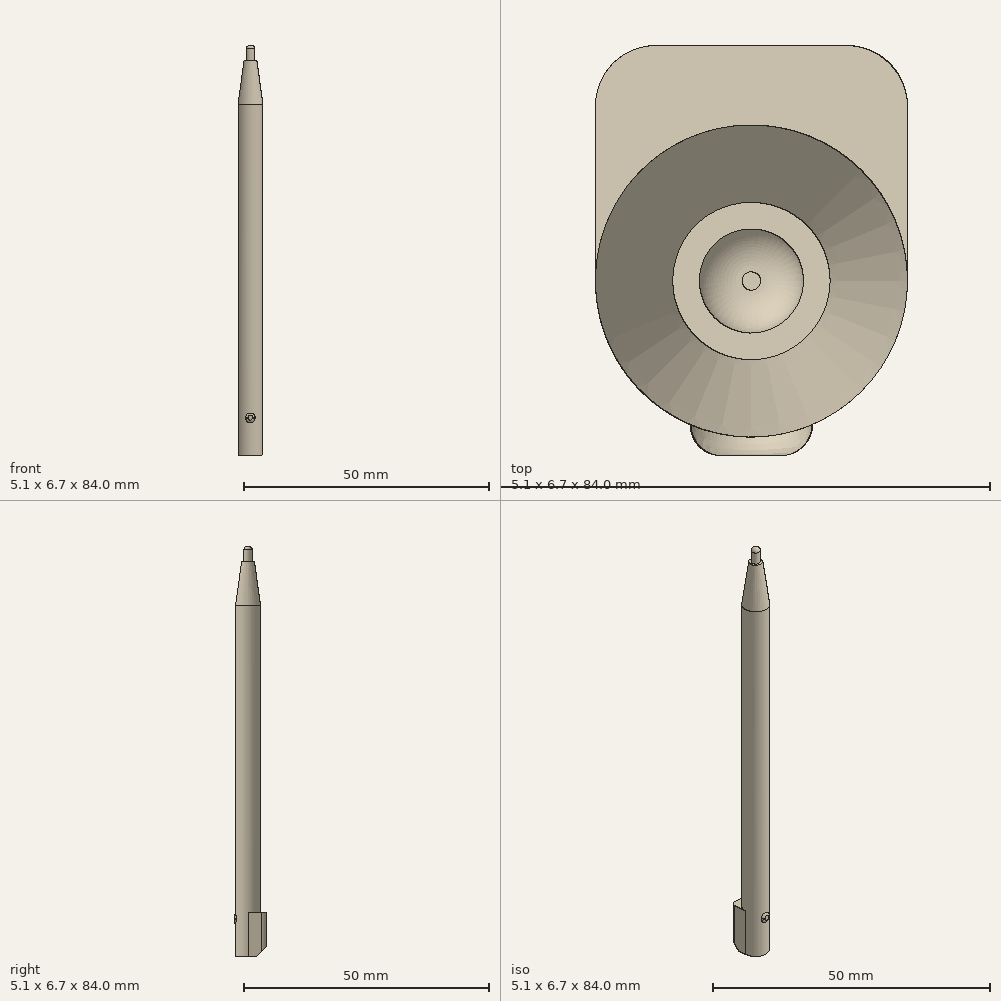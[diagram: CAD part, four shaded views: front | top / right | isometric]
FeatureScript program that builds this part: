
annotation { "Feature Type Name" : "Feature", "Feature Type Description" : "" }
export const myFeature = defineFeature(function(context is Context, id is Id, definition is map)
    precondition{}
    {
        {
            var Q0;
            Q0=qCreatedBy(makeId("Top.planeOp"),FACE);
            var sketch = newSketch(context, id + "F0", { "sketchPlane" : qUnion([Q0])});
            skCircle(sketch, "E0", {"center": v(0, 0) * mm, "radius": 2.55 * mm});
            skLineSegment(sketch, "E1", {"start": v(-2.55, 3.85) * mm, "end": v(2.55, 3.85) * mm});
            skLineSegment(sketch, "E2", {"start": v(2.55, 3.85) * mm, "end": v(2.55, 0) * mm});
            skLineSegment(sketch, "E3", {"start": v(-2.55, 0) * mm, "end": v(-2.55, 3.85) * mm});
            skArc(sketch, "E4", {"start": v(-2.55, 0) * mm, "mid": v(0, -2.55) * mm, "end": v(2.55, 0) * mm});
            skCircle(sketch, "E5", {"center": v(0, 0) * mm, "radius": 0.85 * mm});
            skPoint(sketch, "E6.startSnap0", {"position": v(0, -2.55) * mm});
            skLineSegment(sketch, "E7", {"start": v(0, -2.65) * mm, "end": v(0, -3.76) * mm, "construction": true});
            skSolve(sketch);
        }
        {
            var Q0;
            Q0=makeQuery(id+"F0.imprint","IMPRINT",FACE,{"disambiguationData":[TD([[makeQuery(id+"F0.imprint","IMPRINT",EDGE,{"derivedFrom":sQuery(id+"F0.wireOp",EDGE,"E1")}),-1.0]])]});
            var Q1;
            Q1=makeQuery(id+"F0.imprint","IMPRINT",FACE,{"disambiguationData":[TD([[makeQuery(id+"F0.imprint","IMPRINT",EDGE,{"derivedFrom":sQuery(id+"F0.wireOp",EDGE,"E5")}),1.0]])]});
            var Q2;
            Q2=makeQuery(id+"F0.imprint","IMPRINT",FACE,{"disambiguationData":[TD([[makeQuery(id+"F0.imprint","IMPRINT",EDGE,{"derivedFrom":sQuery(id+"F0.wireOp",EDGE,"E5")}),-1.0]])]});
            extrude(context, id + "F1", {"entities" : qUnion([Q0, Q1, Q2]), "oppositeDirection" : true, "depth" : 9 * mm, "offsetDistance" : 25 * mm});
        }
        {
            var Q0;
            {var subQ0=sQuery(id+"F0.wireOp",EDGE,"E0");var subQ1=makeQuery(id+"F0.imprint","INTERSECT",VERTEX,{"derivedFrom":[subQ0,sQuery(id+"F0.wireOp",EDGE,"E2")]});Q0=makeQuery(id+"F0.imprint","IMPRINT",FACE,{"disambiguationData":[TD([[makeQuery(id+"F0.imprint","IMPRINT",EDGE,{"disambiguationData":[TD([[subQ1,1.0]])],"derivedFrom":subQ0}),1.0]])]});}
            var Q1;
            Q1=makeQuery(id+"F0.imprint","IMPRINT",FACE,{"disambiguationData":[TD([[makeQuery(id+"F0.imprint","IMPRINT",EDGE,{"derivedFrom":sQuery(id+"F0.wireOp",EDGE,"E5")}),1.0]])]});
            extrude(context, id + "F2", {"entities" : qUnion([Q0, Q1]), "operationType" : NewBodyOperationType.ADD, "depth" : 63 * mm, "offsetDistance" : 25 * mm});
        }
        {
            var Q0;
            Q0=makeQuery(id+"F2.opExtrude","CAP_FACE",FACE,{"disambiguationData":[OSD([sQuery(id+"F0.wireOp",EDGE,"E0")])],"isStart":false});
            extrude(context, id + "F3", {"entities" : qUnion([Q0]), "operationType" : NewBodyOperationType.ADD, "depth" : 9 * mm, "offsetDistance" : 25 * mm, "hasDraft" : true, "draftAngle" : 8 * degree, "draftPullDirection" : true});
        }
        {
            var Q0;
            Q0=makeQuery(id+"F1.opExtrude","SWEPT_EDGE",EDGE,{"disambiguationData":[OSD([sQuery(id+"F0.wireOp",EDGE,"E1"),sQuery(id+"F0.wireOp",EDGE,"E2")])]});
            var Q1;
            Q1=makeQuery(id+"F1.opExtrude","SWEPT_EDGE",EDGE,{"disambiguationData":[OSD([sQuery(id+"F0.wireOp",EDGE,"E1"),sQuery(id+"F0.wireOp",EDGE,"E3")])]});
            fillet(context, id + "F4", {"entities" : qUnion([Q0, Q1]), "radius" : 1 * mm, "tangentPropagation" : true, "allowEdgeOverflow" : false});
        }
        {
            var Q0;
            Q0=makeQuery(id+"F0.imprint","IMPRINT",FACE,{"disambiguationData":[TD([[makeQuery(id+"F0.imprint","IMPRINT",EDGE,{"derivedFrom":sQuery(id+"F0.wireOp",EDGE,"E5")}),1.0]])]});
            extrude(context, id + "F5", {"entities" : qUnion([Q0]), "operationType" : NewBodyOperationType.ADD, "depth" : 75 * mm, "offsetDistance" : 25 * mm});
        }
        {
            var Q0;
            Q0=makeQuery(id+"F5.opExtrude","CAP_EDGE",EDGE,{"disambiguationData":[OSD([sQuery(id+"F0.wireOp",EDGE,"E5")])],"isStart":false});
            fillet(context, id + "F6", {"entities" : qUnion([Q0]), "radius" : 0.7 * mm, "tangentPropagation" : true, "allowEdgeOverflow" : false});
        }
        {
            var Q0;
            Q0=makeQuery(id+"F1.opExtrude","SWEPT_FACE",FACE,{"disambiguationData":[OSD([sQuery(id+"F0.wireOp",EDGE,"E1")])]});
            var sketch = newSketch(context, id + "F7", { "sketchPlane" : qUnion([Q0])});
            skCircle(sketch, "E8", {"center": v(0, -1.3) * mm, "radius": 1 * mm});
            skSolve(sketch);
        }
        {
            var Q0;
            Q0 = qSketchRegion(id + "F7", true);
            var Q1;
            {var subQ0=sQuery(id+"F0.wireOp",EDGE,"E0");Q1=makeQuery(id+"F2.boolean.opBoolean","MERGE",FACE,{"derivedFrom":[makeQuery(id+"F1.opExtrude","SWEPT_FACE",FACE,{"disambiguationData":[OSD([subQ0])]}),makeQuery(id+"F2.opExtrude","SWEPT_FACE",FACE,{"disambiguationData":[OSD([subQ0])]})]});}
            extrude(context, id + "F8", {"entities" : qUnion([Q0]), "operationType" : NewBodyOperationType.ADD, "oppositeDirection" : true, "depth" : 6.7 * mm, "offsetDistance" : 25 * mm, "hasSecondDirection" : true, "secondDirectionBound" : SecondDirectionBoundingType.UP_TO_SURFACE, "secondDirectionOppositeDirection" : true, "secondDirectionDepth" : 25 * mm, "secondDirectionBoundEntityFace" : qUnion([Q1])});
        }
        {
            var Q0;
            {var subQ0=sQuery(id+"F7.wireOp",EDGE,"E8");var subQ1=makeQuery(id+"F1.opExtrude","SWEPT_EDGE",EDGE,{"disambiguationData":[OSD([sQuery(id+"F0.wireOp",EDGE,"E0"),sQuery(id+"F0.wireOp",EDGE,"E2")])]});var subQ2=makeQuery(id+"F7.imprint","INTERSECT",VERTEX,{"disambiguationData":[OD(0.0)],"derivedFrom":[subQ1,subQ0]});Q0=makeQuery(id+"F8.opExtrude","CAP_EDGE",EDGE,{"disambiguationData":[OSD([subQ0]),topologyDisambiguationEdgeConnected([makeQuery(id+"F7.imprint","IMPRINT",EDGE,{"disambiguationData":[TD([[subQ2,1.0]])],"derivedFrom":subQ0})])],"isStart":false});}
            fillet(context, id + "F9", {"entities" : qUnion([Q0]), "radius" : 0.5 * mm, "tangentPropagation" : true, "allowEdgeOverflow" : false});
        }
        {
            var Q0;
            Q0=makeQuery(id+"F1.opExtrude","CAP_EDGE",EDGE,{"disambiguationData":[OSD([sQuery(id+"F0.wireOp",EDGE,"E1")])],"isStart":false});
            chamfer(context, id + "F10", {"entities" : qUnion([Q0]), "width" : 2 * mm});
        }
    });
